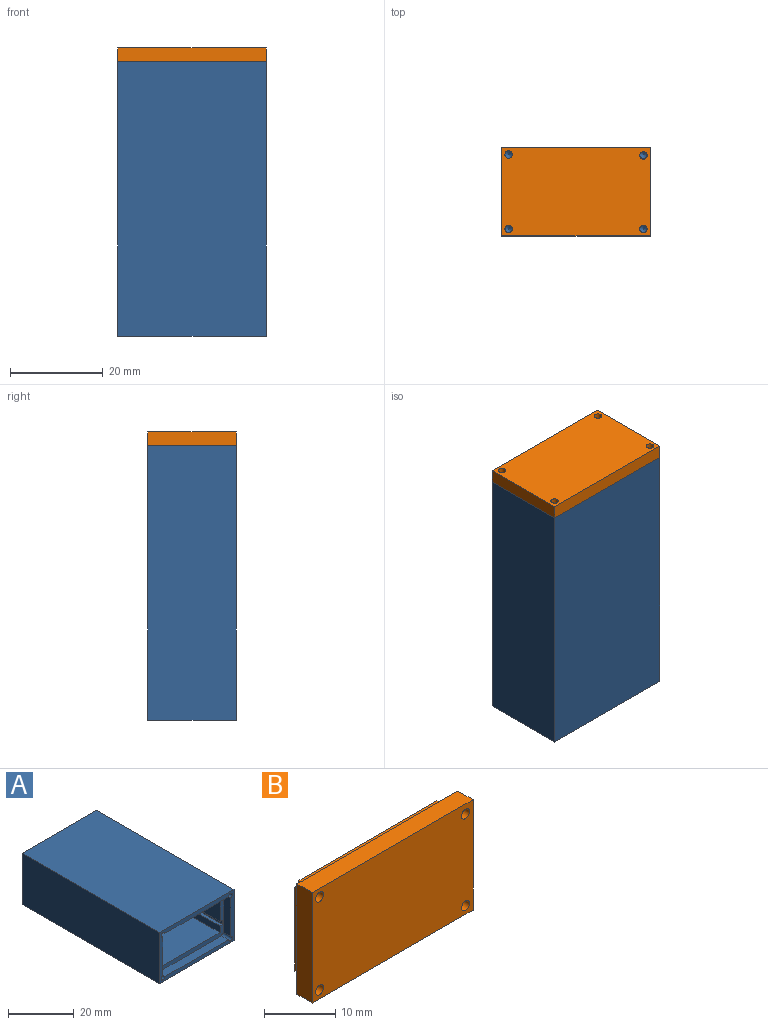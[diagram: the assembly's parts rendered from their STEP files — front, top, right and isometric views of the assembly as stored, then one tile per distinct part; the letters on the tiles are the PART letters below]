
ASSEMBLY  parts=2 mates=1
PART A: 32 faces, bbox 32x59x19 mm
  f0: plane 32x19mm, normal (0,-1,0), area 138mm2, adj f1,f2,f3,f4,f17,f18,f19,f20
  f1: plane 27.4x3mm, normal (0,0,1), area 82.2mm2, adj f0,f21,f28,f30
  f2: plane 14.4x3mm, normal (-1,0,0), area 43.2mm2, adj f0,f21,f27,f30
  f3: plane 14.4x3mm, normal (1,0,0), area 43.2mm2, adj f0,f21,f25,f28
  f4: plane 27.4x3mm, normal (0,0,-1), area 82.2mm2, adj f0,f21,f25,f27
  f5: plane 53x1mm, normal (0,0,-1), area 53mm2, adj f6,f16,f21,f22
  f6: plane 53x8.9mm, normal (1,0,0), area 471.7mm2, adj f5,f7,f21,f22
  f7: plane 53x26mm, normal (0,0,-1), area 1378mm2, adj f6,f8,f21,f22
  f8: plane 53x8.9mm, normal (-1,0,0), area 471.7mm2, adj f7,f9,f21,f22
  f9: plane 53x1mm, normal (0,0,-1), area 53mm2, adj f8,f10,f21,f22
  f10: plane 53x1.6mm, normal (-1,0,0), area 84.8mm2, adj f9,f11,f21,f22
  f11: plane 53x1mm, normal (0,0,1), area 53mm2, adj f10,f12,f21,f22
  f12: plane 53x2.5mm, normal (-1,0,0), area 132.5mm2, adj f11,f13,f21,f22
  f13: plane 53x26mm, normal (0,0,1), area 1378mm2, adj f12,f14,f21,f22
  f14: plane 53x2.5mm, normal (1,0,0), area 132.5mm2, adj f13,f15,f21,f22
  f15: plane 53x1mm, normal (0,0,1), area 53mm2, adj f14,f16,f21,f22
  f16: plane 53x1.6mm, normal (1,0,0), area 84.8mm2, adj f5,f15,f21,f22
  f17: plane 59x32mm, normal (0,0,1), area 1888mm2, adj f0,f18,f20,f23
  f18: plane 59x19mm, normal (-1,0,0), area 1121mm2, adj f0,f17,f19,f23
  f19: plane 59x32mm, normal (0,0,-1), area 1888mm2, adj f0,f18,f20,f23
  f20: plane 59x19mm, normal (1,0,0), area 1121mm2, adj f0,f17,f19,f23
  f21: plane 29x16mm, normal (0,-1,0), area 120.8mm2, adj f1,f2,f3,f4,f5,f6,f7,f8
  f22: plane 28x13mm, normal (0,-1,0), area 341.2mm2, adj f5,f6,f7,f8,f9,f10,f11,f12
  f23: plane 32x19mm, normal (0,1,0), area 608mm2, adj f17,f18,f19,f20
  f24: cone r=0mm half-angle=59deg, axis (0,-1,0), area 2.3mm2, adj f25
  f25: cylinder r=0.8mm len=8mm, axis (0,-1,0), area 36.4mm2, adj f0,f3,f4,f21,f24
  f26: cone r=0mm half-angle=59deg, axis (0,-1,0), area 2.3mm2, adj f27
  f27: cylinder r=0.8mm len=8mm, axis (0,-1,0), area 36.4mm2, adj f0,f2,f4,f21,f26
  f28: cylinder r=0.8mm len=8mm, axis (0,-1,0), area 36.4mm2, adj f0,f1,f3,f21,f29
  f29: cone r=0mm half-angle=59deg, axis (0,-1,0), area 2.3mm2, adj f28
  f30: cylinder r=0.8mm len=8mm, axis (0,-1,0), area 36.4mm2, adj f0,f1,f2,f21,f31
  f31: cone r=0mm half-angle=59deg, axis (0,-1,0), area 2.3mm2, adj f30
PART B: 15 faces, bbox 32x4.9x19 mm
  f0: plane 14.2x1.9mm, normal (1,0,0), area 27mm2, adj f9,f10,f13,f14
  f1: plane 27.4x1.9mm, normal (0,0,-1), area 52.1mm2, adj f9,f10,f12,f14
  f2: plane 27.43x1.9mm, normal (0,0,1), area 52.1mm2, adj f9,f10,f11,f13
  f3: plane 14.4x1.9mm, normal (-1,0,0), area 27.4mm2, adj f9,f10,f11,f12
  f4: plane 32x3mm, normal (0,0,1), area 96mm2, adj f5,f7,f8,f9
  f5: plane 19x3mm, normal (-1,0,0), area 57mm2, adj f4,f6,f8,f9
  f6: plane 32x3mm, normal (0,0,-1), area 96mm2, adj f5,f7,f8,f9
  f7: plane 19x3mm, normal (1,0,0), area 57mm2, adj f4,f6,f8,f9
  f8: plane 32x19mm, normal (0,-1,0), area 600mm2, adj f4,f5,f6,f7,f11,f12,f13,f14
  f9: plane 32x19mm, normal (0,1,0), area 138.1mm2, adj f0,f1,f2,f3,f4,f5,f6,f7
  f10: plane 29x16mm, normal (0,1,0), area 461.8mm2, adj f0,f1,f2,f3,f11,f12,f13,f14
  f11: cylinder r=0.8mm len=4.9mm, axis (0,-1,0), area 17.5mm2, adj f2,f3,f8,f9,f10
  f12: cylinder r=0.8mm len=4.9mm, axis (0,-1,0), area 17.5mm2, adj f1,f3,f8,f9,f10
  f13: cylinder r=0.8mm len=4.9mm, axis (0,-1,0), area 17.9mm2, adj f0,f2,f8,f9,f10
  f14: cylinder r=0.8mm len=4.9mm, axis (0,-1,0), area 17.5mm2, adj f0,f1,f8,f9,f10
PLACE A rot(axis=(-1,0,0),90deg) t=(23.77,-29.87,-56.09)mm
PLACE B rot(axis=(-1,0,0),90deg) t=(75.75,-63.39,-0.09)mm
MATE planar B.f9 <-> A.f0  axis (0,0,-1) through (40.55,-39.35,-0.09)mm
